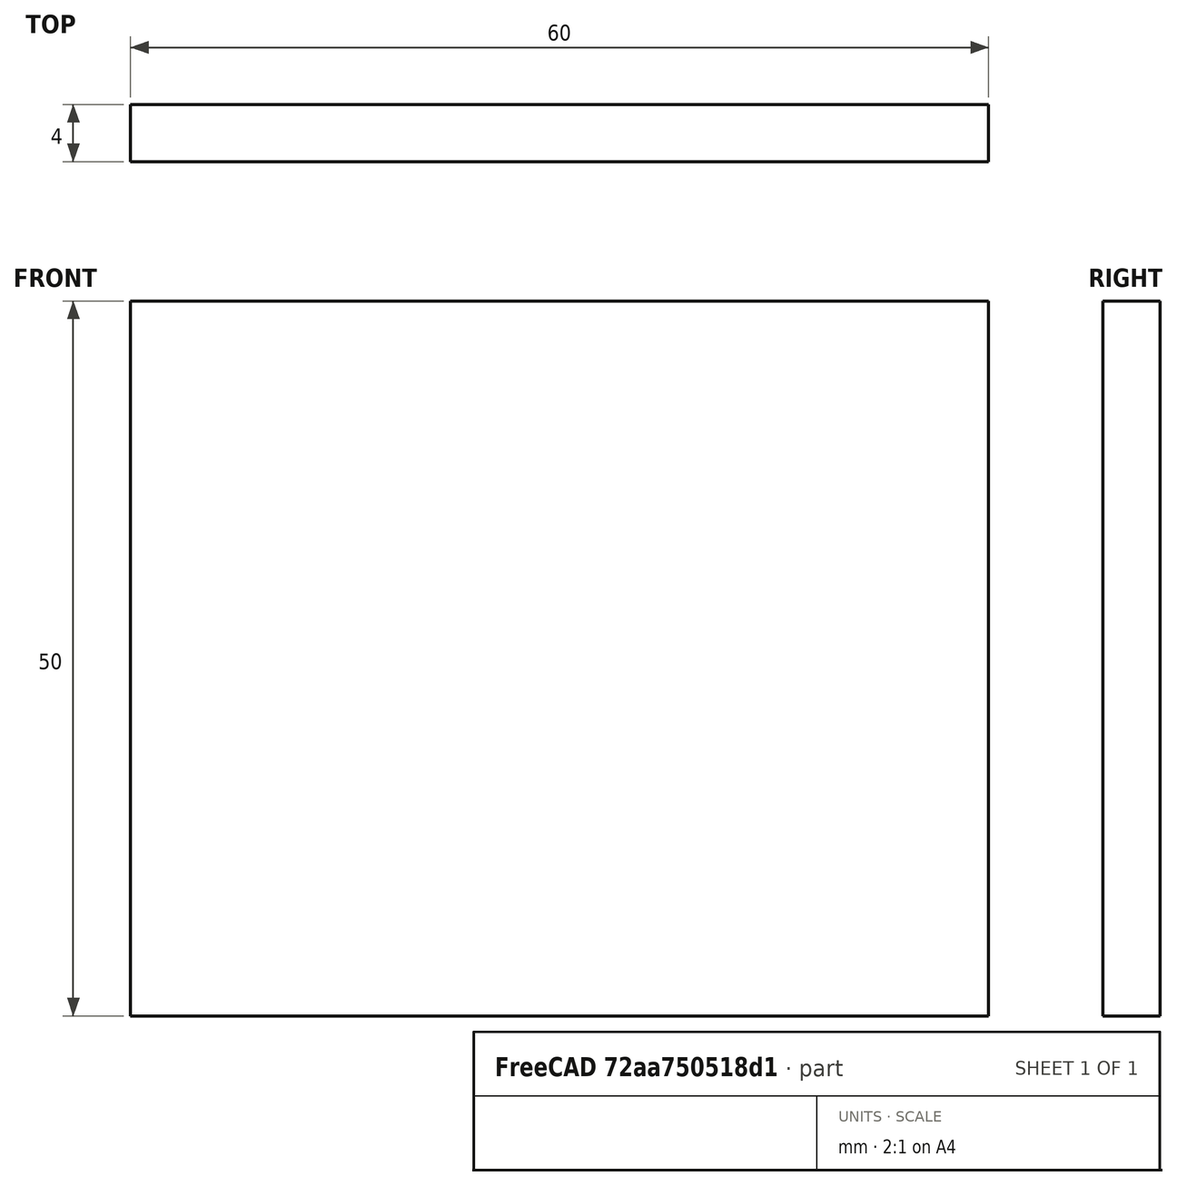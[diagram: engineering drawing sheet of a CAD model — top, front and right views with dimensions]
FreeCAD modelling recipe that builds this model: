
FCSTD DOCUMENT  (FreeCAD 0.15R4671 (Git))
Label: Flat Bar 60x4 EN10058 S235JR
License: All rights reserved
LicenseURL: http://en.wikipedia.org/wiki/All_rights_reserved
objects: Sketcher::SketchObject×1, Part::Extrusion×1
note: 2 computed .brp shape members not serialized (recipe doc carries the construction recipe); baked Part::Feature solids carry a one-line shape summary decoded from their .brp

FEATURE [Sketcher::SketchObject] Sketch
  sketch-geometry (4):
    g0: LineSegment StartX=-30 StartY=-2 StartZ=0 EndX=30 EndY=-2 EndZ=0
    g1: LineSegment StartX=30 StartY=-2 StartZ=0 EndX=30 EndY=2 EndZ=0
    g2: LineSegment StartX=30 StartY=2 StartZ=0 EndX=-30 EndY=2 EndZ=0
    g3: LineSegment StartX=-30 StartY=2 StartZ=0 EndX=-30 EndY=-2 EndZ=0
  constraints (12):
    c: Coincident(g0,g1)
    c: Coincident(g1,g2)
    c: Coincident(g2,g3)
    c: Coincident(g3,g0)
    c: Horizontal(g0)
    c: Horizontal(g2)
    c: Vertical(g1)
    c: Vertical(g3)
    c: Symmetric(g1,g2,g-2)
    c: Symmetric(g0,g1,g-1)
    c: DistanceY(g1) = 4
    c: DistanceX(g0) = 60
FEATURE [Part::Extrusion] Extrude  label="Flat Bar 60x4 EN10058 S235JR"
  Base = -> Sketch
  Dir = (0,0,50)
  Solid = true
